# Revit family: V-08PPFL8_60Hz
name_source: partatom
category: 機械設備
units: mm (PartAtom-declared; Revit-internal decimal feet)

## family parameters
OmniClass タイトル = Axial Fans
OmniClass 番号 = 23.75.35.17.24
パーツ タイプ = 標準
ロード時にボイドで切り取り = いいえ
丸型コネクタ寸法 = 直径を使用
作業面ベース = いいえ
共有 = いいえ
常に垂直 = はい
部屋計算ポイント = はい

## types (1)
- V-08PPFL8
    D1 = 90
    Depth = 30
    EAサイズ_D = 95
    H1 = 80
    Height = 165
    IfcExportAs = IfcFanType
    IfcExportType = TUBEAXIAL
    MAX静圧 = 0.0 Pa
    MAX風量 = 120.0 m³/h
    MID静圧 = 0.0 Pa
    MID風量 = 0.0 m³/h
    MIN静圧 = 0.0 Pa
    MIN風量 = 70.0 m³/h
    OmniClassCode = 23-33 31 19 11
    URL = https://www.mitsubishielectric.co.jp
    Uniclass2015Code = Pr_65_67_29_05
    Uniclass2015Title = Axial flow fans
    Uniclass2015Version = Systems v1.9
    W1 = 250
    Width = 160  [stored 0.524934 ft]
    ダクト径 = 100 mm
    マテリアル = 合成樹脂(白)
    モデル = V-08PPFL8
    仕様書バージョン = Version1.0
    企業コード = 108420
    価格 = 14900 $
    分類コード = 50052503100070
    周波数 = 60 Hz
    呼称 = パイプファン
    極数 = 2
    法定耐用年数 = 15
    消費電力 = 5 W
    相 = 1
    積算_科目 = 2 換気設備
    羽根径 = ∅85
    製品リリース年月 = 2022年6月1日
    製品出荷対象 = 国内
    製品質量 = 0.57 kg
    製造元 = 三菱電機株式会社
    設置方法 = 壁付
    説明 = パイプ用ファン 角形格子タイプ
    負荷分類 = 3_ファン類
    質量 = 0.68 kg
    運転質量 = 0.00 kg
    電動機出力 = 0 W
    電圧 = 100 V

note: [stored X ft] marks values corroborated as IEEE doubles in the binary element streams (Revit-internal decimal feet)
